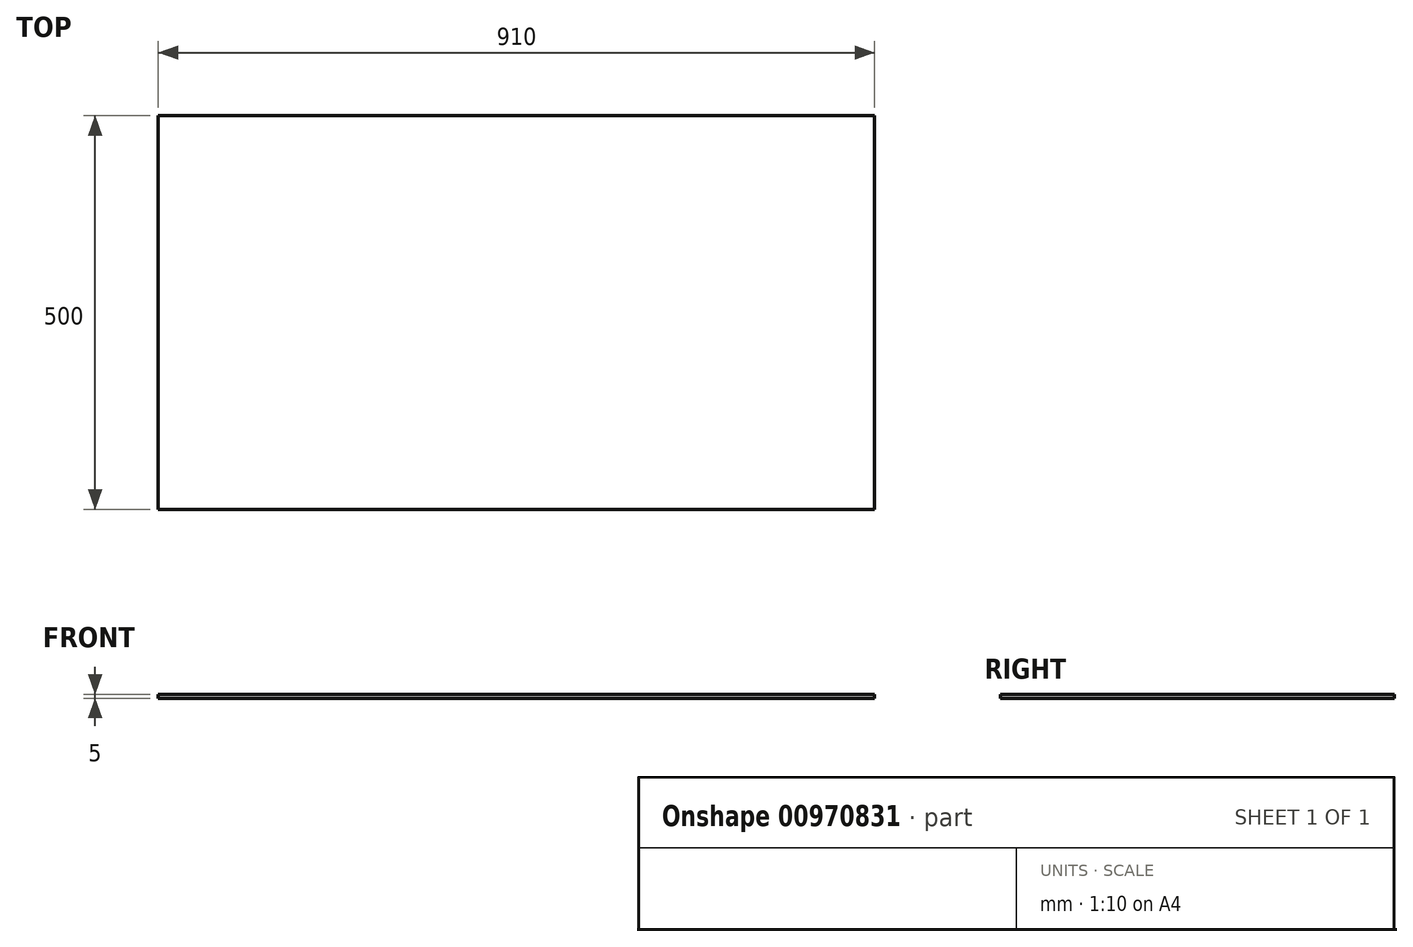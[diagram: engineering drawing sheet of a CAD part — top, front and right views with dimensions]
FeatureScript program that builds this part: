
annotation { "Feature Type Name" : "Feature", "Feature Type Description" : "" }
export const myFeature = defineFeature(function(context is Context, id is Id, definition is map)
    precondition{}
    {
        {
            var Q0;
            Q0=qCreatedBy(makeId("Top.planeOp"),FACE);
            var sketch = newSketch(context, id + "F0", { "sketchPlane" : qUnion([Q0])});
            skLineSegment(sketch, "E0.bottom", {"start": v(-744.03, 65.48) * mm, "end": v(165.97, 65.48) * mm});
            skLineSegment(sketch, "E0.top", {"start": v(-744.03, -434.52) * mm, "end": v(165.97, -434.52) * mm});
            skLineSegment(sketch, "E0.left", {"start": v(-744.03, 65.48) * mm, "end": v(-744.03, -434.52) * mm});
            skLineSegment(sketch, "E0.right", {"start": v(165.97, 65.48) * mm, "end": v(165.97, -434.52) * mm});
            skSolve(sketch);
        }
        {
            var Q0;
            Q0=qSketchRegion(id+"F0",true);
            extrude(context, id + "F1", {"entities" : qUnion([Q0]), "depth" : 5 * mm, "offsetDistance" : 25 * mm});
        }
    });
